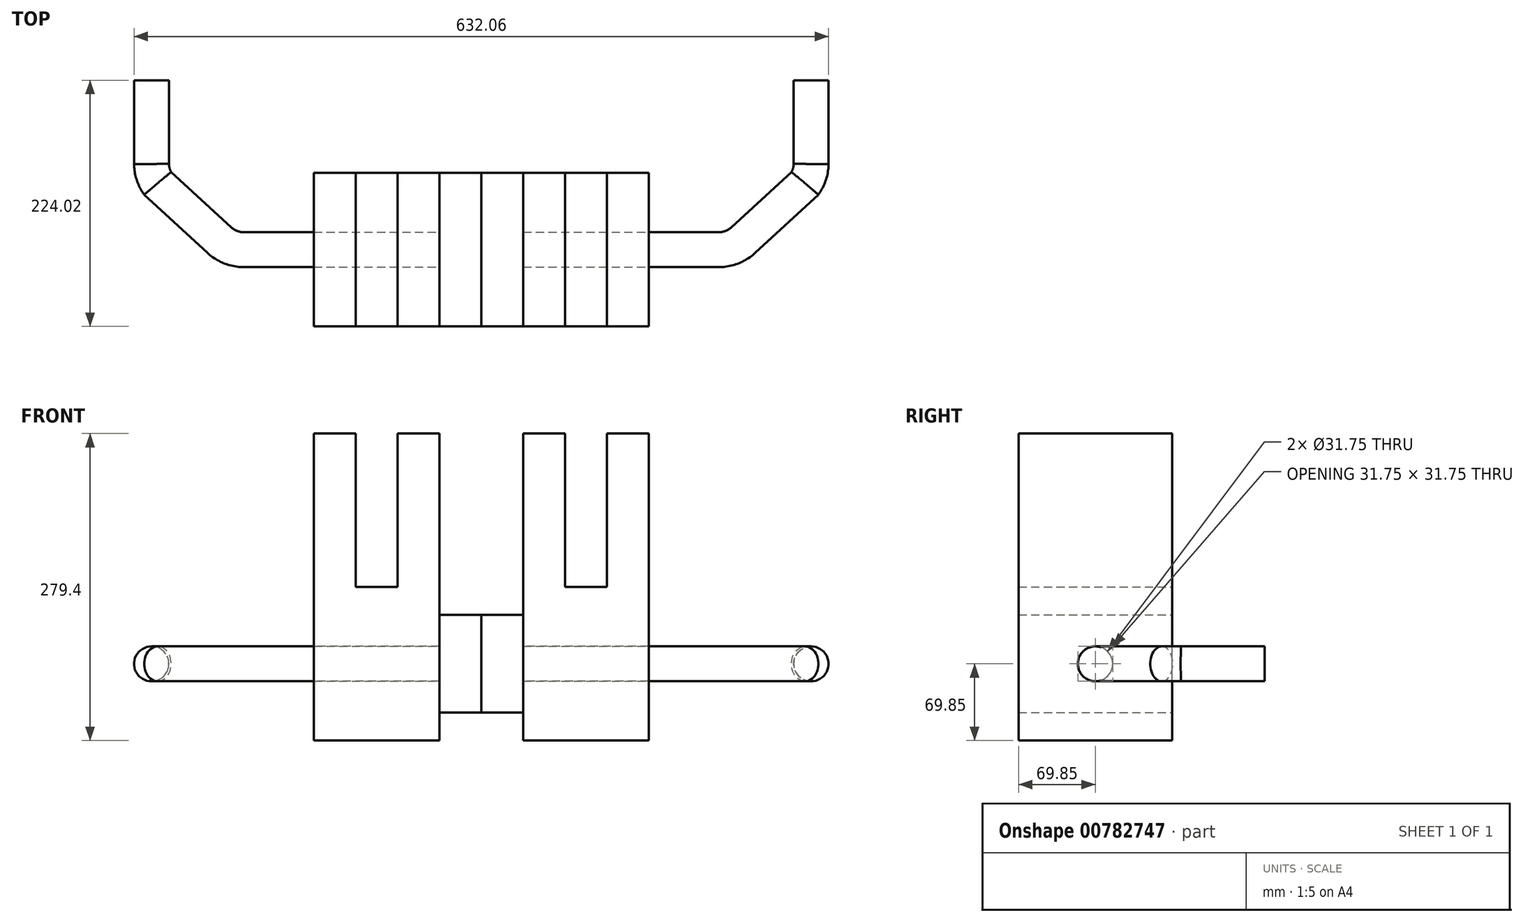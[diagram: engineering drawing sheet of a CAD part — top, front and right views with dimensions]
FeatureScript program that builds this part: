
annotation { "Feature Type Name" : "Feature", "Feature Type Description" : "" }
export const myFeature = defineFeature(function(context is Context, id is Id, definition is map)
    precondition{}
    {
        {
            var Q0;
            Q0=qCreatedBy(makeId("Right.planeOp"),FACE);
            var sketch = newSketch(context, id + "F0", { "sketchPlane" : qUnion([Q0])});
            skCircle(sketch, "E0", {"center": v(0, 0) * mm, "radius": 15.88 * mm});
            skSolve(sketch);
        }
        {
            var Q0;
            Q0=qCreatedBy(makeId("Top.planeOp"),FACE);
            var sketch = newSketch(context, id + "F1", { "sketchPlane" : qUnion([Q0])});
            skLineSegment(sketch, "E1", {"start": v(0, 0) * mm, "end": v(215.9, 0) * mm});
            skArc(sketch, "E2", {"start": v(215.9, 0) * mm, "mid": v(228.05, 2.29) * mm, "end": v(238.53, 8.83) * mm});
            skLineSegment(sketch, "E3", {"start": v(238.53, 8.83) * mm, "end": v(294.58, 60.45) * mm});
            skArc(sketch, "E4", {"start": v(294.58, 60.45) * mm, "mid": v(298.6, 68.82) * mm, "end": v(300.15, 77.97) * mm});
            skLineSegment(sketch, "E5", {"start": v(300.15, 77.97) * mm, "end": v(300.15, 154.17) * mm});
            skSolve(sketch);
        }
        {
            var Q0;
            Q0=makeQuery(id+"F0.imprint","IMPRINT",FACE,{"disambiguationData":[TD([[makeQuery(id+"F0.imprint","IMPRINT",EDGE,{"derivedFrom":sQuery(id+"F0.wireOp",EDGE,"E0")}),1.0]])]});
            var Q1;
            Q1=sQuery(id+"F1.wireOp",EDGE,"E1");
            var Q2;
            Q2=sQuery(id+"F1.wireOp",EDGE,"E2");
            var Q3;
            Q3=sQuery(id+"F1.wireOp",EDGE,"E3");
            var Q4;
            Q4=sQuery(id+"F1.wireOp",EDGE,"E4");
            var Q5;
            Q5=sQuery(id+"F1.wireOp",EDGE,"E5");
            sweep(context, id + "F2", {"profiles" : qUnion([Q0]), "path" : qUnion([Q1, Q2, Q3, Q4, Q5])});
        }
        {
            var Q0;
            Q0=makeQuery(id+"F2.opSweep","CAP_FACE",FACE,{"disambiguationData":[OSD([sQuery(id+"F0.wireOp",EDGE,"E0"),sQuery(id+"F1.wireOp",VERTEX,"E1.start")])],"isStart":true});
            var sketch = newSketch(context, id + "F3", { "sketchPlane" : qUnion([Q0])});
            skLineSegment(sketch, "E6.bottom", {"start": v(69.85, -69.85) * mm, "end": v(-69.85, -69.85) * mm});
            skLineSegment(sketch, "E6.top", {"start": v(69.85, 69.85) * mm, "end": v(-69.85, 69.85) * mm});
            skLineSegment(sketch, "E6.left", {"start": v(69.85, -69.85) * mm, "end": v(69.85, 69.85) * mm});
            skLineSegment(sketch, "E6.right", {"start": v(-69.85, -69.85) * mm, "end": v(-69.85, 69.85) * mm});
            skPoint(sketch, "E6.middle", {"position": v(0, 0) * mm});
            skSolve(sketch);
        }
        {
            var Q0;
            Q0=makeQuery(id+"F3.imprint","IMPRINT",FACE,{"disambiguationData":[TD([[makeQuery(id+"F3.imprint","IMPRINT",EDGE,{"derivedFrom":makeQuery(id+"F2.opSweep","CAP_EDGE",EDGE,{"disambiguationData":[OSD([sQuery(id+"F0.wireOp",EDGE,"E0"),sQuery(id+"F1.wireOp",VERTEX,"E1.start")])],"isStart":true})}),-1.0]])]});
            var sketch = newSketch(context, id + "F4", { "sketchPlane" : qUnion([Q0])});
            skLineSegment(sketch, "E7.bottom", {"start": v(69.85, -69.85) * mm, "end": v(-69.85, -69.85) * mm});
            skLineSegment(sketch, "E7.top", {"start": v(69.85, 69.85) * mm, "end": v(-69.85, 69.85) * mm});
            skLineSegment(sketch, "E7.left", {"start": v(69.85, -69.85) * mm, "end": v(69.85, 69.85) * mm});
            skLineSegment(sketch, "E7.right", {"start": v(-69.85, -69.85) * mm, "end": v(-69.85, 69.85) * mm});
            skPoint(sketch, "E7.middle", {"position": v(0, 0) * mm});
            skSolve(sketch);
        }
        {
            var Q0;
            Q0 = qSketchRegion(id + "F4", true);
            extrude(context, id + "F5", {"entities" : qUnion([Q0]), "operationType" : NewBodyOperationType.ADD, "oppositeDirection" : true, "depth" : 38.1 * mm, "offsetDistance" : 25.4 * mm});
        }
        {
            var Q0;
            Q0=makeQuery(id+"F5.opExtrude","CAP_FACE",FACE,{"disambiguationData":[OSD([sQuery(id+"F4.wireOp",EDGE,"E7.bottom"),sQuery(id+"F4.wireOp",EDGE,"E7.top"),sQuery(id+"F4.wireOp",EDGE,"E7.left"),sQuery(id+"F4.wireOp",EDGE,"E7.right")])],"isStart":false});
            extrude(context, id + "F6", {"entities" : qUnion([Q0]), "depth" : 38.1 * mm, "offsetDistance" : 25.4 * mm});
        }
        {
            var Q0;
            Q0=makeQuery(id+"F6.opExtrude","CAP_FACE",FACE,{"disambiguationData":[OSD([sQuery(id+"F4.wireOp",EDGE,"E7.bottom"),sQuery(id+"F4.wireOp",EDGE,"E7.top"),sQuery(id+"F4.wireOp",EDGE,"E7.left"),sQuery(id+"F4.wireOp",EDGE,"E7.right")])],"isStart":false});
            extrude(context, id + "F7", {"entities" : qUnion([Q0]), "depth" : 38.1 * mm, "offsetDistance" : 25.4 * mm});
        }
        {
            var Q0;
            Q0=makeQuery(id+"F7.opExtrude","CAP_FACE",FACE,{"disambiguationData":[OSD([sQuery(id+"F4.wireOp",EDGE,"E7.bottom"),sQuery(id+"F4.wireOp",EDGE,"E7.top"),sQuery(id+"F4.wireOp",EDGE,"E7.left"),sQuery(id+"F4.wireOp",EDGE,"E7.right")])],"isStart":false});
            extrude(context, id + "F8", {"entities" : qUnion([Q0]), "depth" : 38.1 * mm, "offsetDistance" : 25.4 * mm});
        }
        {
            var Q0;
            Q0=makeQuery(id+"F5.opExtrude","SWEPT_FACE",FACE,{"disambiguationData":[OSD([sQuery(id+"F4.wireOp",EDGE,"E7.top")])]});
            extrude(context, id + "F9", {"entities" : qUnion([Q0]), "operationType" : NewBodyOperationType.REMOVE, "oppositeDirection" : true, "depth" : 25.4 * mm, "offsetDistance" : 25.4 * mm});
        }
        {
            var Q0;
            Q0=makeQuery(id+"F5.opExtrude","SWEPT_FACE",FACE,{"disambiguationData":[OSD([sQuery(id+"F4.wireOp",EDGE,"E7.bottom")])]});
            extrude(context, id + "F10", {"entities" : qUnion([Q0]), "operationType" : NewBodyOperationType.REMOVE, "oppositeDirection" : true, "depth" : 25.4 * mm, "offsetDistance" : 25.4 * mm});
        }
        {
            var Q0;
            Q0=makeQuery(id+"F6.opExtrude","SWEPT_FACE",FACE,{"disambiguationData":[OSD([sQuery(id+"F4.wireOp",EDGE,"E7.top")])]});
            extrude(context, id + "F11", {"entities" : qUnion([Q0]), "operationType" : NewBodyOperationType.ADD, "depth" : 139.7 * mm, "offsetDistance" : 25.4 * mm});
        }
        {
            var Q0;
            Q0=makeQuery(id+"F8.opExtrude","SWEPT_FACE",FACE,{"disambiguationData":[OSD([sQuery(id+"F4.wireOp",EDGE,"E7.top")])]});
            extrude(context, id + "F12", {"entities" : qUnion([Q0]), "operationType" : NewBodyOperationType.ADD, "depth" : 139.7 * mm, "offsetDistance" : 25.4 * mm});
        }
        {
            var Q0;
            Q0=makeQuery(id+"F2.opSweep","SWEPT_BODY",BODY,{"disambiguationData":[OSD([sQuery(id+"F0.wireOp",EDGE,"E0"),sQuery(id+"F1.wireOp",EDGE,"E5")])]});
            var Q1;
            Q1=makeQuery(id+"F6.opExtrude","SWEPT_BODY",BODY,{"disambiguationData":[OSD([sQuery(id+"F4.wireOp",EDGE,"E7.bottom"),sQuery(id+"F4.wireOp",EDGE,"E7.top"),sQuery(id+"F4.wireOp",EDGE,"E7.left"),sQuery(id+"F4.wireOp",EDGE,"E7.right")])]});
            var Q2;
            Q2=makeQuery(id+"F7.opExtrude","SWEPT_BODY",BODY,{"disambiguationData":[OSD([sQuery(id+"F4.wireOp",EDGE,"E7.bottom"),sQuery(id+"F4.wireOp",EDGE,"E7.top"),sQuery(id+"F4.wireOp",EDGE,"E7.left"),sQuery(id+"F4.wireOp",EDGE,"E7.right")])]});
            var Q3;
            Q3=makeQuery(id+"F8.opExtrude","SWEPT_BODY",BODY,{"disambiguationData":[OSD([sQuery(id+"F4.wireOp",EDGE,"E7.bottom"),sQuery(id+"F4.wireOp",EDGE,"E7.top"),sQuery(id+"F4.wireOp",EDGE,"E7.left"),sQuery(id+"F4.wireOp",EDGE,"E7.right")])]});
            var Q4;
            Q4=makeQuery(id+"F3.imprint","IMPRINT",FACE,{"disambiguationData":[TD([[makeQuery(id+"F3.imprint","IMPRINT",EDGE,{"derivedFrom":sQuery(id+"F3.wireOp",EDGE,"E6.bottom")}),-1.0]])]});
            mirror(context, id + "F13", {"entities" : qUnion([Q0, Q1, Q2, Q3]), "mirrorPlane" : qUnion([Q4])});
        }
    });
